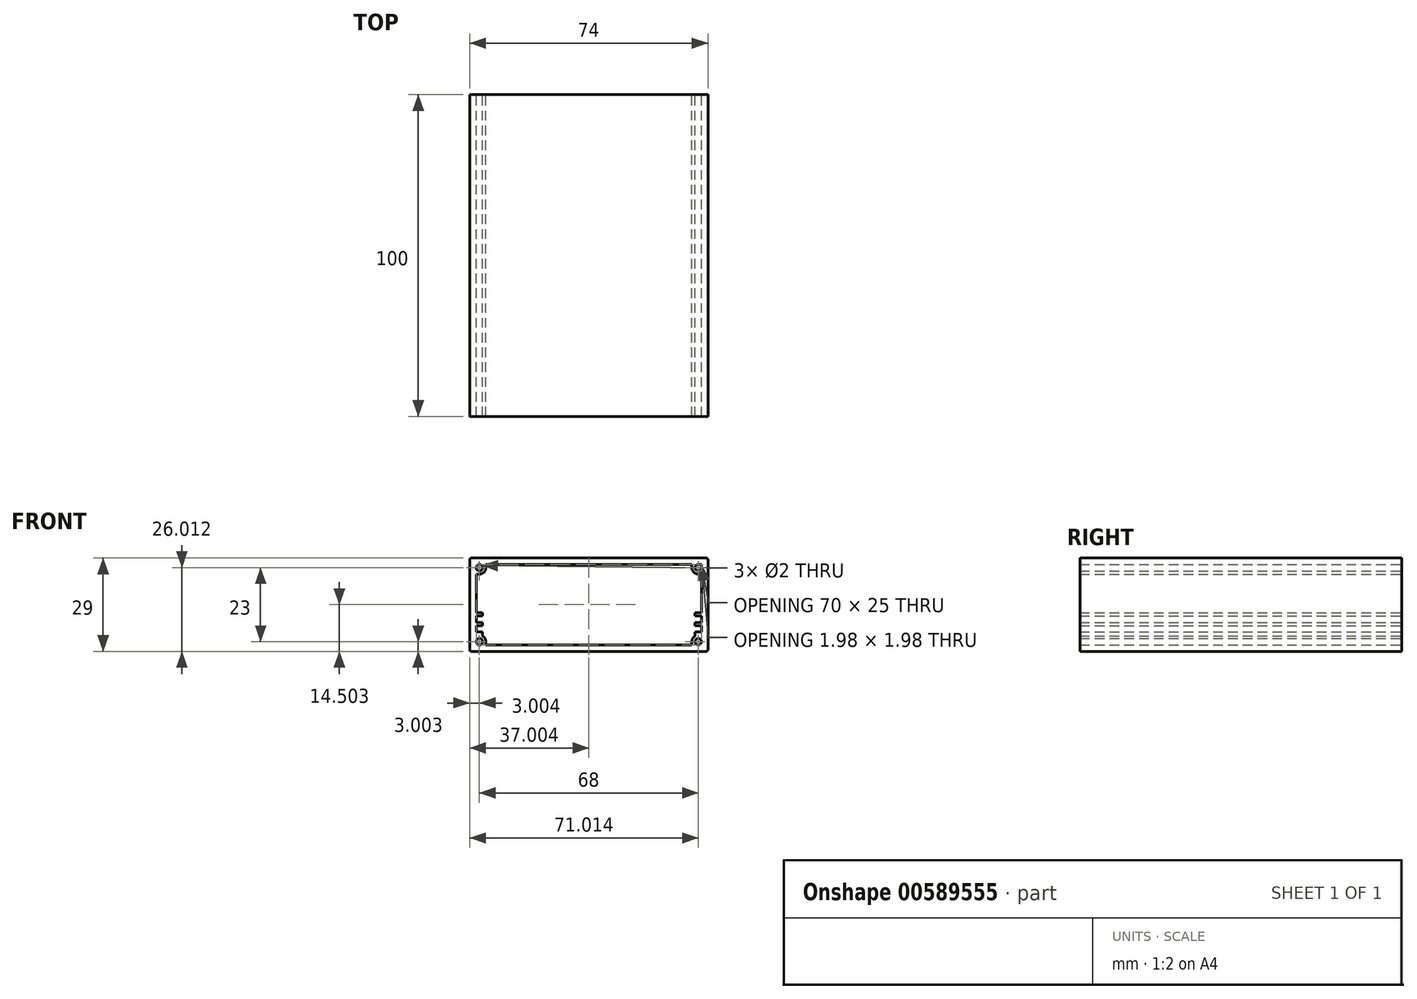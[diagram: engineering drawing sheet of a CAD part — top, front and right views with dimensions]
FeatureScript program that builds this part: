
annotation { "Feature Type Name" : "Feature", "Feature Type Description" : "" }
export const myFeature = defineFeature(function(context is Context, id is Id, definition is map)
    precondition{}
    {
        {
            var Q0;
            Q0=qCreatedBy(makeId("Front.planeOp"),FACE);
            var sketch = newSketch(context, id + "F0", { "sketchPlane" : qUnion([Q0])});
            skLineSegment(sketch, "E0.bottom", {"start": v(-35.56, 14.65) * mm, "end": v(37.44, 14.65) * mm});
            skLineSegment(sketch, "E0.top", {"start": v(-35.56, -14.35) * mm, "end": v(37.44, -14.35) * mm});
            skLineSegment(sketch, "E0.left", {"start": v(-36.06, 14.15) * mm, "end": v(-36.06, -13.85) * mm});
            skLineSegment(sketch, "E0.right", {"start": v(37.94, 14.15) * mm, "end": v(37.94, -13.85) * mm});
            skPoint(sketch, "E1", {"position": v(-33.06, 11.65) * mm});
            skLineSegment(sketch, "E2", {"start": v(-37.06, 0.15) * mm, "end": v(38.94, 0.15) * mm, "construction": true});
            skLineSegment(sketch, "E3", {"start": v(0.94, 15.65) * mm, "end": v(0.94, -15.35) * mm, "construction": true});
            skPoint(sketch, "E4.MirrorP", {"position": v(-33.06, -11.35) * mm});
            skPoint(sketch, "E5.MirrorP", {"position": v(34.94, 11.65) * mm});
            skPoint(sketch, "E6.MirrorP", {"position": v(34.94, -11.35) * mm});
            skCircle(sketch, "E7", {"center": v(-33.06, -11.35) * mm, "radius": 1.5 * mm, "construction": true});
            skPoint(sketch, "E8.visualSharp", {"position": v(37.94, 14.65) * mm});
            skArc(sketch, "E8.filletArc", {"start": v(37.94, 14.15) * mm, "mid": v(37.8, 14.5) * mm, "end": v(37.44, 14.65) * mm});
            skPoint(sketch, "E9.visualSharp", {"position": v(37.94, -14.35) * mm});
            skArc(sketch, "E9.filletArc", {"start": v(37.44, -14.35) * mm, "mid": v(37.8, -14.2) * mm, "end": v(37.94, -13.85) * mm});
            skPoint(sketch, "E10.visualSharp", {"position": v(-36.06, 14.65) * mm});
            skArc(sketch, "E10.filletArc", {"start": v(-35.56, 14.65) * mm, "mid": v(-35.9, 14.5) * mm, "end": v(-36.06, 14.15) * mm});
            skPoint(sketch, "E11.visualSharp", {"position": v(-36.06, -14.35) * mm});
            skArc(sketch, "E11.filletArc", {"start": v(-36.06, -13.85) * mm, "mid": v(-35.9, -14.2) * mm, "end": v(-35.56, -14.35) * mm});
            skCircle(sketch, "E12.0.1.0", {"center": v(-33.06, 11.65) * mm, "radius": 1.5 * mm, "construction": true});
            skCircle(sketch, "E12.1.0.0", {"center": v(34.94, -11.35) * mm, "radius": 1.5 * mm, "construction": true});
            skCircle(sketch, "E12.1.1.0", {"center": v(34.94, 11.65) * mm, "radius": 1.5 * mm, "construction": true});
            skLineSegment(sketch, "E12.direction1", {"start": v(-33.06, -11.35) * mm, "end": v(34.94, -11.35) * mm, "construction": true});
            skLineSegment(sketch, "E12.direction2", {"start": v(-33.06, -11.35) * mm, "end": v(-33.06, 11.65) * mm, "construction": true});
            skLineSegment(sketch, "E13.bottom", {"start": v(35.94, 12.65) * mm, "end": v(-34.06, 12.65) * mm});
            skLineSegment(sketch, "E13.top", {"start": v(35.94, -12.35) * mm, "end": v(-34.06, -12.35) * mm});
            skLineSegment(sketch, "E13.left", {"start": v(35.94, 12.65) * mm, "end": v(35.94, -12.35) * mm});
            skLineSegment(sketch, "E13.right", {"start": v(-34.06, 12.65) * mm, "end": v(-34.06, -12.35) * mm});
            skLineSegment(sketch, "E14.bottom", {"start": v(35.94, 12.65) * mm, "end": v(32.94, 12.65) * mm});
            skLineSegment(sketch, "E14.top", {"start": v(35.94, 9.65) * mm, "end": v(34.94, 9.65) * mm});
            skLineSegment(sketch, "E14.left", {"start": v(35.94, 12.65) * mm, "end": v(35.94, 9.65) * mm});
            skLineSegment(sketch, "E14.right", {"start": v(32.94, 12.65) * mm, "end": v(32.94, 11.65) * mm});
            skPoint(sketch, "E15.visualSharp", {"position": v(32.94, 9.65) * mm});
            skArc(sketch, "E15.filletArc", {"start": v(32.94, 11.65) * mm, "mid": v(33.53, 10.24) * mm, "end": v(34.94, 9.65) * mm});
            skLineSegment(sketch, "E16.MirrorCS", {"start": v(-34.06, 9.65) * mm, "end": v(-33.06, 9.65) * mm});
            skLineSegment(sketch, "E17.MirrorCS", {"start": v(-31.06, 12.65) * mm, "end": v(-31.06, 11.65) * mm});
            skArc(sketch, "E18.MirrorCS", {"start": v(-31.06, 11.65) * mm, "mid": v(-31.64, 10.24) * mm, "end": v(-33.06, 9.65) * mm});
            skLineSegment(sketch, "E19.MirrorCS", {"start": v(35.94, -9.35) * mm, "end": v(34.94, -9.35) * mm});
            skPoint(sketch, "E20.MirrorP", {"position": v(32.94, -9.35) * mm});
            skArc(sketch, "E21.MirrorCS", {"start": v(32.94, -11.35) * mm, "mid": v(33.53, -9.93) * mm, "end": v(34.94, -9.35) * mm});
            skLineSegment(sketch, "E22.MirrorCS", {"start": v(32.94, -12.35) * mm, "end": v(32.94, -11.35) * mm});
            skArc(sketch, "E23.MirrorCS", {"start": v(-31.06, -11.35) * mm, "mid": v(-31.64, -9.93) * mm, "end": v(-33.06, -9.35) * mm});
            skLineSegment(sketch, "E24.MirrorCS", {"start": v(-31.06, -12.35) * mm, "end": v(-31.06, -11.35) * mm});
            skLineSegment(sketch, "E25.MirrorCS", {"start": v(-33.06, 11.65) * mm, "end": v(-33.06, -11.35) * mm, "construction": true});
            skLineSegment(sketch, "E26.MirrorCS", {"start": v(-34.06, -9.35) * mm, "end": v(-33.06, -9.35) * mm});
            skLineSegment(sketch, "E27.bottom", {"start": v(35.94, -8.35) * mm, "end": v(33.94, -8.35) * mm});
            skLineSegment(sketch, "E27.top", {"start": v(35.94, -8.35) * mm, "end": v(33.94, -8.35) * mm});
            skLineSegment(sketch, "E27.left", {"start": v(35.94, -8.35) * mm, "end": v(35.94, -8.35) * mm});
            skLineSegment(sketch, "E27.right", {"start": v(33.94, -8.35) * mm, "end": v(33.94, -8.35) * mm});
            skLineSegment(sketch, "E28.bottom", {"start": v(35.94, -5.35) * mm, "end": v(33.94, -5.35) * mm});
            skLineSegment(sketch, "E28.top", {"start": v(35.94, -6.35) * mm, "end": v(33.94, -6.35) * mm});
            skLineSegment(sketch, "E28.left", {"start": v(35.94, -5.35) * mm, "end": v(35.94, -6.35) * mm});
            skLineSegment(sketch, "E28.right", {"start": v(33.94, -5.35) * mm, "end": v(33.94, -6.35) * mm});
            skCircle(sketch, "E29", {"center": v(34.94, -11.35) * mm, "radius": 1 * mm});
            skCircle(sketch, "E30.MirrorC", {"center": v(34.94, 11.65) * mm, "radius": 1 * mm});
            skCircle(sketch, "E31.MirrorC", {"center": v(-33.06, 11.65) * mm, "radius": 1 * mm});
            skCircle(sketch, "E32.MirrorC", {"center": v(-33.06, -11.35) * mm, "radius": 1 * mm});
            skLineSegment(sketch, "E33", {"start": v(33.94, -8.35) * mm, "end": v(33.94, -9.62) * mm});
            skLineSegment(sketch, "E34.MirrorCS", {"start": v(-32.06, -8.35) * mm, "end": v(-32.06, -9.62) * mm});
            skLineSegment(sketch, "E35.MirrorCS", {"start": v(-34.06, -8.35) * mm, "end": v(-32.06, -8.35) * mm});
            skLineSegment(sketch, "E36.MirrorCS", {"start": v(-34.06, -6.35) * mm, "end": v(-32.06, -6.35) * mm});
            skLineSegment(sketch, "E37.MirrorCS", {"start": v(-34.06, -5.35) * mm, "end": v(-32.06, -5.35) * mm});
            skLineSegment(sketch, "E38.MirrorCS", {"start": v(-32.06, -5.35) * mm, "end": v(-32.06, -6.35) * mm});
            skLineSegment(sketch, "E39.bottom", {"start": v(35.94, -2.35) * mm, "end": v(33.94, -2.35) * mm});
            skLineSegment(sketch, "E39.top", {"start": v(35.94, -3.35) * mm, "end": v(33.94, -3.35) * mm});
            skLineSegment(sketch, "E39.left", {"start": v(35.94, -2.35) * mm, "end": v(35.94, -3.35) * mm});
            skLineSegment(sketch, "E39.right", {"start": v(33.94, -2.35) * mm, "end": v(33.94, -3.35) * mm});
            skLineSegment(sketch, "E40.MirrorCS", {"start": v(-34.06, -2.35) * mm, "end": v(-32.06, -2.35) * mm});
            skLineSegment(sketch, "E41.MirrorCS", {"start": v(-32.06, -2.35) * mm, "end": v(-32.06, -3.35) * mm});
            skLineSegment(sketch, "E42.MirrorCS", {"start": v(-34.06, -3.35) * mm, "end": v(-32.06, -3.35) * mm});
            skSolve(sketch);
        }
        {
            var Q0;
            {var subQ2=sQuery(id+"F0.wireOp",EDGE,"E14.top");Q0=makeQuery(id+"F0.imprint","IMPRINT",FACE,{"disambiguationData":[TD([[makeQuery(id+"F0.imprint","IMPRINT",EDGE,{"derivedFrom":subQ2}),-1.0]])]});}
            var Q1;
            {var subQ0=sQuery(id+"F0.wireOp",EDGE,"E14.left");var subQ1=sQuery(id+"F0.wireOp",EDGE,"E14.bottom");var subQ2=makeQuery(id+"F0.imprint","INTERSECT",VERTEX,{"derivedFrom":[subQ1,subQ0]});Q1=makeQuery(id+"F0.imprint","IMPRINT",FACE,{"disambiguationData":[TD([[makeQuery(id+"F0.imprint","IMPRINT",EDGE,{"disambiguationData":[TD([[subQ2,-1.0]])],"derivedFrom":subQ1}),1.0]])]});}
            var Q2;
            Q2=makeQuery(id+"F0.imprint","IMPRINT",FACE,{"disambiguationData":[TD([[makeQuery(id+"F0.imprint","IMPRINT",EDGE,{"derivedFrom":sQuery(id+"F0.wireOp",EDGE,"E0.bottom")}),-1.0]])]});
            var Q3;
            Q3=makeQuery(id+"F0.imprint","IMPRINT",FACE,{"disambiguationData":[TD([[makeQuery(id+"F0.imprint","IMPRINT",EDGE,{"derivedFrom":sQuery(id+"F0.wireOp",EDGE,"E28.bottom")}),1.0]])]});
            var Q4;
            {var subQ0=sQuery(id+"F0.wireOp",EDGE,"E19.MirrorCS");Q4=makeQuery(id+"F0.imprint","IMPRINT",FACE,{"disambiguationData":[TD([[makeQuery(id+"F0.imprint","IMPRINT",EDGE,{"derivedFrom":subQ0}),1.0]])]});}
            var Q5;
            {var subQ0=sQuery(id+"F0.wireOp",EDGE,"E13.left");var subQ1=sQuery(id+"F0.wireOp",EDGE,"E13.top");var subQ2=makeQuery(id+"F0.imprint","INTERSECT",VERTEX,{"derivedFrom":[subQ1,subQ0]});Q5=makeQuery(id+"F0.imprint","IMPRINT",FACE,{"disambiguationData":[TD([[makeQuery(id+"F0.imprint","IMPRINT",EDGE,{"disambiguationData":[TD([[subQ2,-1.0]])],"derivedFrom":subQ1}),-1.0]])]});}
            var Q6;
            {var subQ0=sQuery(id+"F0.wireOp",EDGE,"E16.MirrorCS");Q6=makeQuery(id+"F0.imprint","IMPRINT",FACE,{"disambiguationData":[TD([[makeQuery(id+"F0.imprint","IMPRINT",EDGE,{"derivedFrom":subQ0}),1.0]])]});}
            var Q7;
            {var subQ0=sQuery(id+"F0.wireOp",EDGE,"E13.right");var subQ1=sQuery(id+"F0.wireOp",EDGE,"E13.bottom");var subQ2=makeQuery(id+"F0.imprint","INTERSECT",VERTEX,{"derivedFrom":[subQ1,subQ0]});Q7=makeQuery(id+"F0.imprint","IMPRINT",FACE,{"disambiguationData":[TD([[makeQuery(id+"F0.imprint","IMPRINT",EDGE,{"disambiguationData":[TD([[subQ2,1.0]])],"derivedFrom":subQ1}),1.0]])]});}
            var Q8;
            Q8=makeQuery(id+"F0.imprint","IMPRINT",FACE,{"disambiguationData":[TD([[makeQuery(id+"F0.imprint","IMPRINT",EDGE,{"derivedFrom":sQuery(id+"F0.wireOp",EDGE,"E23.MirrorCS")}),1.0]])]});
            var Q9;
            {var subQ0=sQuery(id+"F0.wireOp",EDGE,"E13.right");var subQ1=sQuery(id+"F0.wireOp",EDGE,"E13.top");var subQ2=makeQuery(id+"F0.imprint","INTERSECT",VERTEX,{"derivedFrom":[subQ1,subQ0]});Q9=makeQuery(id+"F0.imprint","IMPRINT",FACE,{"disambiguationData":[TD([[makeQuery(id+"F0.imprint","IMPRINT",EDGE,{"disambiguationData":[TD([[subQ2,1.0]])],"derivedFrom":subQ1}),-1.0]])]});}
            var Q10;
            {var subQ2=sQuery(id+"F0.wireOp",EDGE,"E19.MirrorCS");Q10=makeQuery(id+"F0.imprint","IMPRINT",FACE,{"disambiguationData":[TD([[makeQuery(id+"F0.imprint","IMPRINT",EDGE,{"derivedFrom":subQ2}),-1.0]])]});}
            var Q11;
            {var subQ0=sQuery(id+"F0.wireOp",EDGE,"E36.MirrorCS");Q11=makeQuery(id+"F0.imprint","IMPRINT",FACE,{"disambiguationData":[TD([[makeQuery(id+"F0.imprint","IMPRINT",EDGE,{"derivedFrom":subQ0}),1.0]])]});}
            var Q12;
            {var subQ0=sQuery(id+"F0.wireOp",EDGE,"E26.MirrorCS");Q12=makeQuery(id+"F0.imprint","IMPRINT",FACE,{"disambiguationData":[TD([[makeQuery(id+"F0.imprint","IMPRINT",EDGE,{"derivedFrom":subQ0}),1.0]])]});}
            var Q13;
            {var subQ0=sQuery(id+"F0.wireOp",EDGE,"E40.MirrorCS");Q13=makeQuery(id+"F0.imprint","IMPRINT",FACE,{"disambiguationData":[TD([[makeQuery(id+"F0.imprint","IMPRINT",EDGE,{"derivedFrom":subQ0}),-1.0]])]});}
            var Q14;
            Q14=makeQuery(id+"F0.imprint","IMPRINT",FACE,{"disambiguationData":[TD([[makeQuery(id+"F0.imprint","IMPRINT",EDGE,{"derivedFrom":sQuery(id+"F0.wireOp",EDGE,"E39.bottom")}),1.0]])]});
            extrude(context, id + "F1", {"entities" : qUnion([Q0, Q1, Q2, Q3, Q4, Q5, Q6, Q7, Q8, Q9, Q10, Q11, Q12, Q13, Q14]), "depth" : 100 * mm, "offsetDistance" : 25 * mm});
        }
    });
